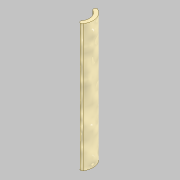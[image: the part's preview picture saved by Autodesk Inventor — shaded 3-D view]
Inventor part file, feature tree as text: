
AUTODESK INVENTOR PART (.ipt)
format: ipt  version: 2021 (Build 250183000, 183)  size: 146,432 bytes
history: native  units: mm
features: fillet x4, extrude x3, sketch x3, sweep x2, projected_geometry x2, other x2, hole x1
ambient origin geometry x8: Origin, YZ Plane, XZ Plane, XY Plane, X Axis, Y Axis, Z Axis, Center Point
bodies: Solid1 (feature_tree)
feature tree (17):
  extrude  "holderProfile"  Depth=3.665191mm
  fillet  "Fillet1"  Radius=2.0mm
  extrude  "holderBase1"  Depth=2.0mm
  fillet  "Fillet2"  Radius=1.0mm
  fillet  "Fillet3"  Radius=70.0mm
  hole  "throughHole"  [1 undecoded]
  sweep  "Sweep1"
  extrude  "Extrusion3"  Depth=1.0mm
  fillet  "Fillet4"  Radius=5.5mm
  sketch  "Sketch1"  dims[d3=12.042772mm d4=3.665191mm d5=2.0mm]
  sketch  "Sketch2"  dims[d6=5.5mm d7=2.0mm d8=1.0mm d9=70.0mm d10=0.0mm]
  projected_geometry  "Projected Loop1"
  other  "throughholePosition"
  sweep  "sweepLine"
  other  "loopProfile"
  sketch  "Sketch7"  dims[d11=1.0mm d12=10.0mm d13=4.0mm d14=0.0mm d15=1.0mm d16=5.5mm d17=3.0mm d18=6.0mm d19=4.0mm d20=2.0mm d21=90.0deg d22=8.0mm d23=0.0mm d26=4.0mm d27=2.0mm d28=0.0mm d29=0.0mm d30=1.75mm d31=0.0mm d32=5.0mm d33=1.0mm]
  projected_geometry  "Projected Loop2"
note: 1 required parameter value undecoded (feature->parameter linkage not recoverable at this tier; creation-order binding heuristic only, values carry confidence <= 0.55)
